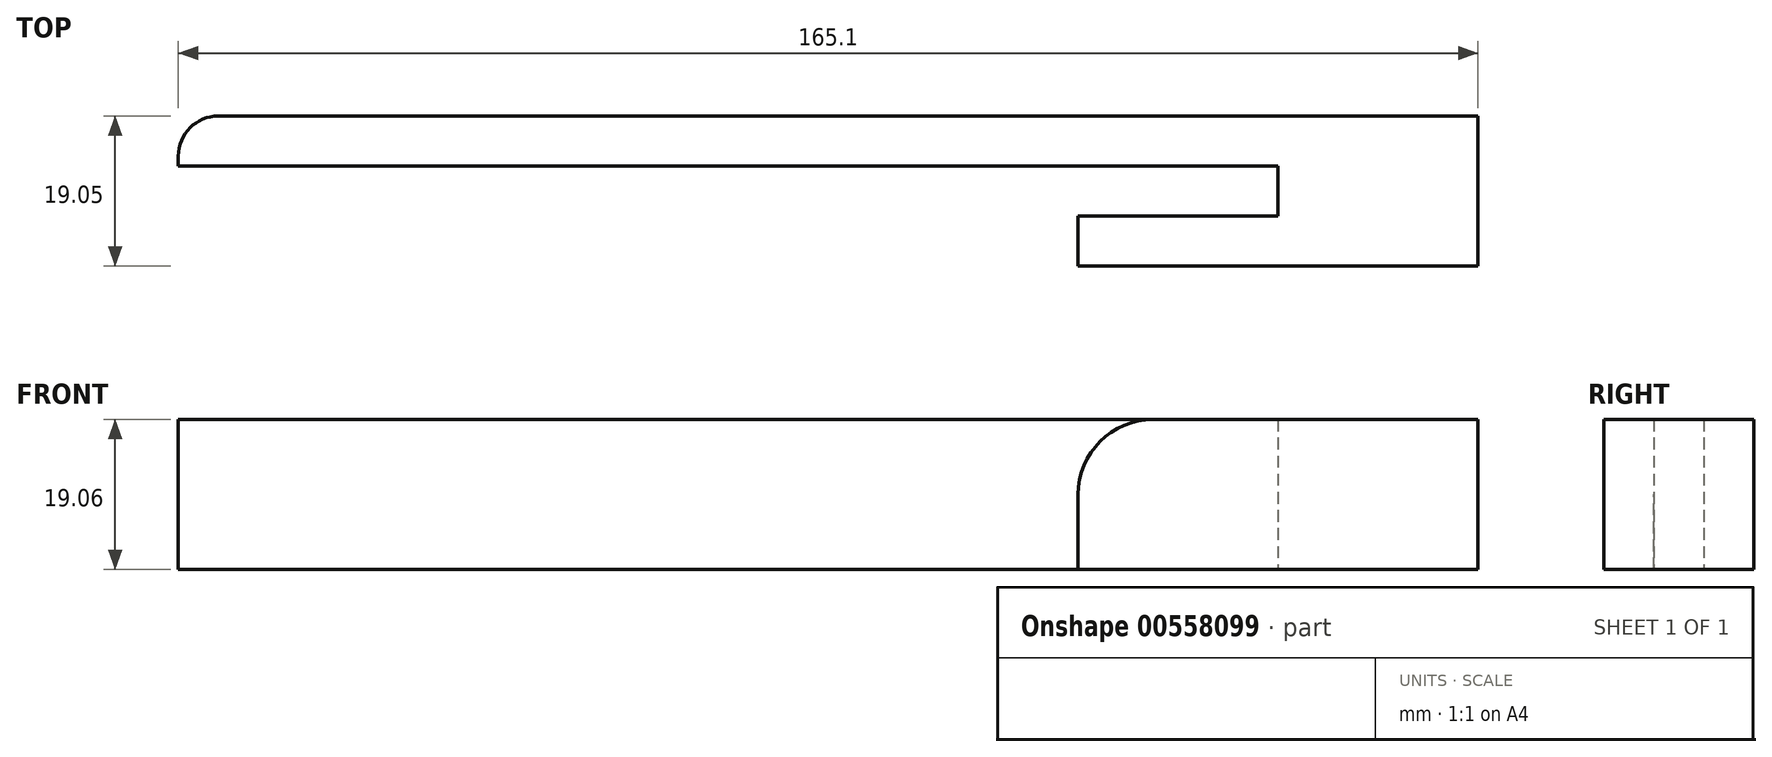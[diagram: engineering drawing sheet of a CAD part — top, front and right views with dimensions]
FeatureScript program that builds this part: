
annotation { "Feature Type Name" : "Feature", "Feature Type Description" : "" }
export const myFeature = defineFeature(function(context is Context, id is Id, definition is map)
    precondition{}
    {
        {
            var Q0;
            Q0=qCreatedBy(makeId("Front.planeOp"),FACE);
            var sketch = newSketch(context, id + "F0", { "sketchPlane" : qUnion([Q0])});
            skLineSegment(sketch, "E0.bottom", {"start": v(9.53, -9.52) * mm, "end": v(-9.52, -9.53) * mm});
            skLineSegment(sketch, "E0.top", {"start": v(9.52, 9.53) * mm, "end": v(0, 9.53) * mm});
            skLineSegment(sketch, "E0.right", {"start": v(-9.52, -9.53) * mm, "end": v(-9.53, 0) * mm});
            skPoint(sketch, "E0.middle", {"position": v(0, 0) * mm});
            skArc(sketch, "E1", {"start": v(0, 9.52) * mm, "mid": v(-6.74, 6.74) * mm, "end": v(-9.52, 0) * mm});
            skPoint(sketch, "E2.orphan", {"position": v(-9.53, 9.52) * mm});
            skLineSegment(sketch, "E3.bottom", {"start": v(9.53, -9.52) * mm, "end": v(41.28, -9.52) * mm});
            skLineSegment(sketch, "E3.top", {"start": v(9.52, 9.53) * mm, "end": v(41.28, 9.53) * mm});
            skLineSegment(sketch, "E3.right", {"start": v(41.28, -9.52) * mm, "end": v(41.27, 9.53) * mm});
            skLineSegment(sketch, "E4.bottom", {"start": v(41.28, 9.53) * mm, "end": v(15.88, 9.53) * mm});
            skLineSegment(sketch, "E4.top", {"start": v(41.28, -9.52) * mm, "end": v(15.88, -9.52) * mm});
            skLineSegment(sketch, "E4.left", {"start": v(41.28, 9.53) * mm, "end": v(41.28, -9.52) * mm});
            skSolve(sketch);
        }
        {
            var Q0;
            Q0 = qSketchRegion(id + "F0", true);
            extrude(context, id + "F1", {"entities" : qUnion([Q0]), "depth" : 6.35 * mm, "offsetDistance" : 25.4 * mm});
        }
        {
            var Q0;
            Q0=qCreatedBy(makeId("Top.planeOp"),FACE);
            var sketch = newSketch(context, id + "F2", { "sketchPlane" : qUnion([Q0])});
            skLineSegment(sketch, "E5.bottom", {"start": v(15.87, 0) * mm, "end": v(41.28, 0) * mm});
            skLineSegment(sketch, "E5.top", {"start": v(15.87, 6.35) * mm, "end": v(41.28, 6.35) * mm});
            skLineSegment(sketch, "E5.right", {"start": v(41.28, 0) * mm, "end": v(41.28, 6.35) * mm});
            skLineSegment(sketch, "E6.right", {"start": v(15.87, 0) * mm, "end": v(15.87, 6.35) * mm});
            skLineSegment(sketch, "E7.bottom", {"start": v(41.28, 6.35) * mm, "end": v(-123.83, 6.35) * mm});
            skLineSegment(sketch, "E7.top", {"start": v(41.27, 12.7) * mm, "end": v(-123.83, 12.7) * mm});
            skLineSegment(sketch, "E7.left", {"start": v(41.28, 6.35) * mm, "end": v(41.28, 12.7) * mm});
            skLineSegment(sketch, "E7.right", {"start": v(-123.83, 6.35) * mm, "end": v(-123.83, 12.7) * mm});
            skSolve(sketch);
        }
        {
            var Q0;
            Q0 = qSketchRegion(id + "F2", true);
            extrude(context, id + "F3", {"entities" : qUnion([Q0]), "operationType" : NewBodyOperationType.ADD, "endBound" : BoundingType.SYMMETRIC, "depth" : 19.05 * mm, "offsetDistance" : 25.4 * mm});
        }
        {
            var Q0;
            Q0=makeQuery(id+"F3.opExtrude","SWEPT_EDGE",EDGE,{"disambiguationData":[OSD([sQuery(id+"F2.wireOp",EDGE,"E7.top"),sQuery(id+"F2.wireOp",EDGE,"E7.right")])]});
            fillet(context, id + "F4", {"entities" : qUnion([Q0]), "radius" : 5.08 * mm, "tangentPropagation" : true, "allowEdgeOverflow" : false});
        }
    });
